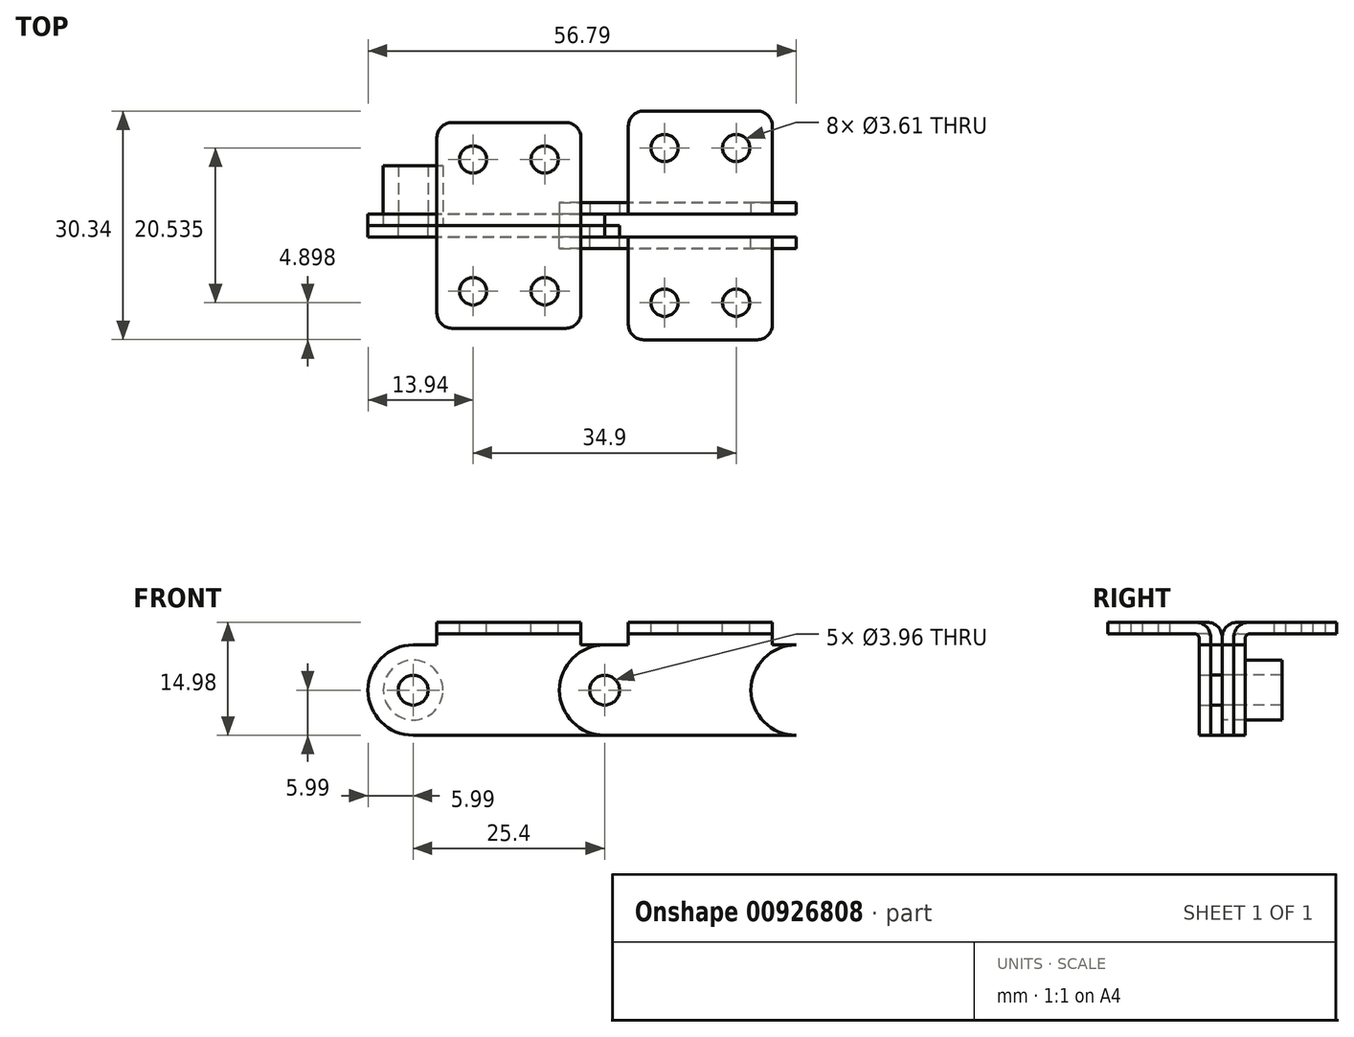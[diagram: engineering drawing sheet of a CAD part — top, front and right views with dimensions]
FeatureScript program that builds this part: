
annotation { "Feature Type Name" : "Feature", "Feature Type Description" : "" }
export const myFeature = defineFeature(function(context is Context, id is Id, definition is map)
    precondition{}
    {
        {
            var Q0;
            Q0=qCreatedBy(makeId("Front.planeOp"),FACE);
            var sketch = newSketch(context, id + "F0", { "sketchPlane" : qUnion([Q0])});
            skCircle(sketch, "E0", {"center": v(-12.7, 0) * mm, "radius": 1.98 * mm});
            skCircle(sketch, "E1", {"center": v(-12.7, 0) * mm, "radius": 6 * mm});
            skLineSegment(sketch, "E2", {"start": v(0, 20.39) * mm, "end": v(0, -19.77) * mm, "construction": true});
            skCircle(sketch, "E3.MirrorC", {"center": v(12.7, 0) * mm, "radius": 1.98 * mm});
            skCircle(sketch, "E4.MirrorC", {"center": v(12.7, 0) * mm, "radius": 6 * mm});
            skLineSegment(sketch, "E5", {"start": v(-12.7, -6) * mm, "end": v(12.7, -6) * mm});
            skLineSegment(sketch, "E6", {"start": v(-12.7, 6) * mm, "end": v(12.7, 6) * mm});
            skSolve(sketch);
        }
        {
            var Q0;
            {var subQ0=sQuery(id+"F0.wireOp",EDGE,"E5");Q0=makeQuery(id+"F0.imprint","IMPRINT",FACE,{"disambiguationData":[TD([[makeQuery(id+"F0.imprint","IMPRINT",EDGE,{"derivedFrom":subQ0}),1.0]])]});}
            var Q1;
            Q1=makeQuery(id+"F0.imprint","IMPRINT",FACE,{"disambiguationData":[TD([[makeQuery(id+"F0.imprint","IMPRINT",EDGE,{"derivedFrom":sQuery(id+"F0.wireOp",EDGE,"E0")}),-1.0]])]});
            var Q2;
            Q2=makeQuery(id+"F0.imprint","IMPRINT",FACE,{"disambiguationData":[TD([[makeQuery(id+"F0.imprint","IMPRINT",EDGE,{"derivedFrom":sQuery(id+"F0.wireOp",EDGE,"E3.MirrorC")}),1.0]])]});
            extrude(context, id + "F1", {"entities" : qUnion([Q0, Q1, Q2]), "depth" : 1.52 * mm, "offsetDistance" : 25 * mm});
        }
        {
            var Q0;
            Q0=qCreatedBy(makeId("Right.planeOp"),FACE);
            var sketch = newSketch(context, id + "F2", { "sketchPlane" : qUnion([Q0])});
            skLineSegment(sketch, "E7.bottom", {"start": v(0, 6) * mm, "end": v(-1.52, 6) * mm});
            skLineSegment(sketch, "E7.right", {"start": v(0, 6) * mm, "end": v(0, 7) * mm});
            skLineSegment(sketch, "E8.bottom", {"start": v(-2.12, 7.47) * mm, "end": v(-13.64, 7.47) * mm});
            skLineSegment(sketch, "E8.top", {"start": v(-2, 9) * mm, "end": v(-13.64, 9) * mm});
            skLineSegment(sketch, "E8.right", {"start": v(-13.64, 9) * mm, "end": v(-13.64, 7.47) * mm});
            skLineSegment(sketch, "E9", {"start": v(-1.52, 6) * mm, "end": v(-1.52, 6.87) * mm});
            skPoint(sketch, "E10.visualSharp", {"position": v(-1.52, 7.47) * mm});
            skArc(sketch, "E10.filletArc", {"start": v(-1.52, 6.87) * mm, "mid": v(-1.7, 7.3) * mm, "end": v(-2.12, 7.47) * mm});
            skArc(sketch, "E11.filletArc", {"start": v(0, 7) * mm, "mid": v(-0.59, 8.4) * mm, "end": v(-2, 9) * mm});
            skSolve(sketch);
        }
        {
            var Q0;
            Q0=makeQuery(id+"F2.imprint","IMPRINT",FACE,{"disambiguationData":[TD([[makeQuery(id+"F2.imprint","IMPRINT",EDGE,{"derivedFrom":sQuery(id+"F2.wireOp",EDGE,"E7.bottom")}),-1.0]])]});
            extrude(context, id + "F3", {"entities" : qUnion([Q0]), "operationType" : NewBodyOperationType.ADD, "endBound" : BoundingType.SYMMETRIC, "depth" : 19.1 * mm, "offsetDistance" : 25 * mm});
        }
        {
            var Q0;
            Q0=makeQuery(id+"F3.opExtrude","SWEPT_FACE",FACE,{"disambiguationData":[OSD([sQuery(id+"F2.wireOp",EDGE,"E8.top")])]});
            var sketch = newSketch(context, id + "F4", { "sketchPlane" : qUnion([Q0])});
            skPoint(sketch, "E12", {"position": v(-4.75, -8.74) * mm});
            skLineSegment(sketch, "E13", {"start": v(0, 6.76) * mm, "end": v(0, -11.23) * mm, "construction": true});
            skPoint(sketch, "E14.MirrorP", {"position": v(4.75, -8.74) * mm});
            skSolve(sketch);
        }
        {
            var Q0;
            Q0=sQuery(id+"F4.wireOp",VERTEX,"E12");
            var Q1;
            Q1=sQuery(id+"F4.wireOp",VERTEX,"E14.MirrorP");
            var Q2;
            Q2=makeQuery(id+"F1.opExtrude","SWEPT_BODY",BODY,{"disambiguationData":[OSD([sQuery(id+"F0.wireOp",EDGE,"E0"),sQuery(id+"F0.wireOp",EDGE,"E1"),sQuery(id+"F0.wireOp",EDGE,"E3.MirrorC"),sQuery(id+"F0.wireOp",EDGE,"E4.MirrorC"),sQuery(id+"F0.wireOp",EDGE,"E5"),sQuery(id+"F0.wireOp",EDGE,"E6")])]});
            hole(context, id + "F5", {"style" : HoleStyle.SIMPLE, "endStyle" : HoleEndStyle.THROUGH, "holeDiameter" : 3.6 * mm, "majorDiameter" : 5 * mm, "isTappedThrough" : true, "tappedDepth" : 12 * mm, "tapClearance" : 3, "startFromSketch" : true, "locations" : qUnion([Q0, Q1]), "scope" : qUnion([Q2])});
        }
        {
            var Q0;
            Q0=makeQuery(id+"F3.opExtrude","CAP_EDGE",EDGE,{"disambiguationData":[OSD([sQuery(id+"F2.wireOp",EDGE,"E8.right")])],"isStart":false});
            var Q1;
            Q1=makeQuery(id+"F3.opExtrude","CAP_EDGE",EDGE,{"disambiguationData":[OSD([sQuery(id+"F2.wireOp",EDGE,"E8.right")])],"isStart":true});
            fillet(context, id + "F6", {"entities" : qUnion([Q0, Q1]), "radius" : 2 * mm, "tangentPropagation" : true, "allowEdgeOverflow" : false});
        }
        {
            var Q0;
            Q0=qCreatedBy(makeId("Front.planeOp"),FACE);
            var sketch = newSketch(context, id + "F7", { "sketchPlane" : qUnion([Q0])});
            skCircle(sketch, "E15", {"center": v(-12.7, 0) * mm, "radius": 3.96 * mm});
            skLineSegment(sketch, "E16", {"start": v(0, 11) * mm, "end": v(0, -16.23) * mm, "construction": true});
            skCircle(sketch, "E17.MirrorC", {"center": v(12.7, 0) * mm, "radius": 3.96 * mm});
            skCircle(sketch, "E18", {"center": v(-12.7, 0) * mm, "radius": 1.98 * mm});
            skCircle(sketch, "E19.MirrorC", {"center": v(12.7, 0) * mm, "radius": 1.98 * mm});
            skSolve(sketch);
        }
        {
            var Q0;
            Q0=makeQuery(id+"F7.imprint","IMPRINT",FACE,{"disambiguationData":[TD([[makeQuery(id+"F7.imprint","IMPRINT",EDGE,{"derivedFrom":sQuery(id+"F7.wireOp",EDGE,"E15")}),1.0]])]});
            var Q1;
            Q1=makeQuery(id+"F7.imprint","IMPRINT",FACE,{"disambiguationData":[TD([[makeQuery(id+"F7.imprint","IMPRINT",EDGE,{"derivedFrom":sQuery(id+"F7.wireOp",EDGE,"E17.MirrorC")}),-1.0]])]});
            extrude(context, id + "F8", {"entities" : qUnion([Q0, Q1]), "oppositeDirection" : true, "depth" : 7.92 * mm, "offsetDistance" : 25 * mm});
        }
        {
            var Q0;
            Q0=qCreatedBy(makeId("Front.planeOp"),FACE);
            cPlane(context, id + "F9", {"entities" : qUnion([Q0]), "cplaneType" : CPlaneType.OFFSET, "offset" : .312 / 50.8 * mm, "oppositeDirection" : true, "width" : 150 * mm, "height" : 150 * mm});
        }
        {
            var Q0;
            Q0=makeQuery(id+"F1.opExtrude","SWEPT_BODY",BODY,{"disambiguationData":[OSD([sQuery(id+"F0.wireOp",EDGE,"E0"),sQuery(id+"F0.wireOp",EDGE,"E1"),sQuery(id+"F0.wireOp",EDGE,"E3.MirrorC"),sQuery(id+"F0.wireOp",EDGE,"E4.MirrorC"),sQuery(id+"F0.wireOp",EDGE,"E5"),sQuery(id+"F0.wireOp",EDGE,"E6")])]});
            var Q1;
            Q1=qCreatedBy(id+"F9.planeOp",FACE);
            mirror(context, id + "F10", {"entities" : qUnion([Q0]), "mirrorPlane" : qUnion([Q1])});
        }
        {
            var Q0;
            Q0=makeQuery(id+"F1.opExtrude","SWEPT_BODY",BODY,{"disambiguationData":[OSD([sQuery(id+"F0.wireOp",EDGE,"E0"),sQuery(id+"F0.wireOp",EDGE,"E1"),sQuery(id+"F0.wireOp",EDGE,"E3.MirrorC"),sQuery(id+"F0.wireOp",EDGE,"E4.MirrorC"),sQuery(id+"F0.wireOp",EDGE,"E5"),sQuery(id+"F0.wireOp",EDGE,"E6")])]});
            transform(context, id + "F11", {"entities" : qUnion([Q0]), "transformType" : TransformType.TRANSLATION_3D, "dx" : 25.4 * mm, "dy" : -1.52 * mm, "dz" : 0 * mm, "makeCopy" : true});
        }
        {
            var Q0;
            Q0=makeQuery(id+"F10.opPattern","COPY",BODY,{"derivedFrom":makeQuery(id+"F1.opExtrude","SWEPT_BODY",BODY,{"disambiguationData":[OSD([sQuery(id+"F0.wireOp",EDGE,"E0"),sQuery(id+"F0.wireOp",EDGE,"E1"),sQuery(id+"F0.wireOp",EDGE,"E3.MirrorC"),sQuery(id+"F0.wireOp",EDGE,"E4.MirrorC"),sQuery(id+"F0.wireOp",EDGE,"E5"),sQuery(id+"F0.wireOp",EDGE,"E6")])]}),"instanceName":"1"});
            transform(context, id + "F12", {"entities" : qUnion([Q0]), "transformType" : TransformType.TRANSLATION_3D, "dx" : 25.4 * mm, "dy" : 1.52 * mm, "dz" : 0 * mm, "makeCopy" : true});
        }
    });
